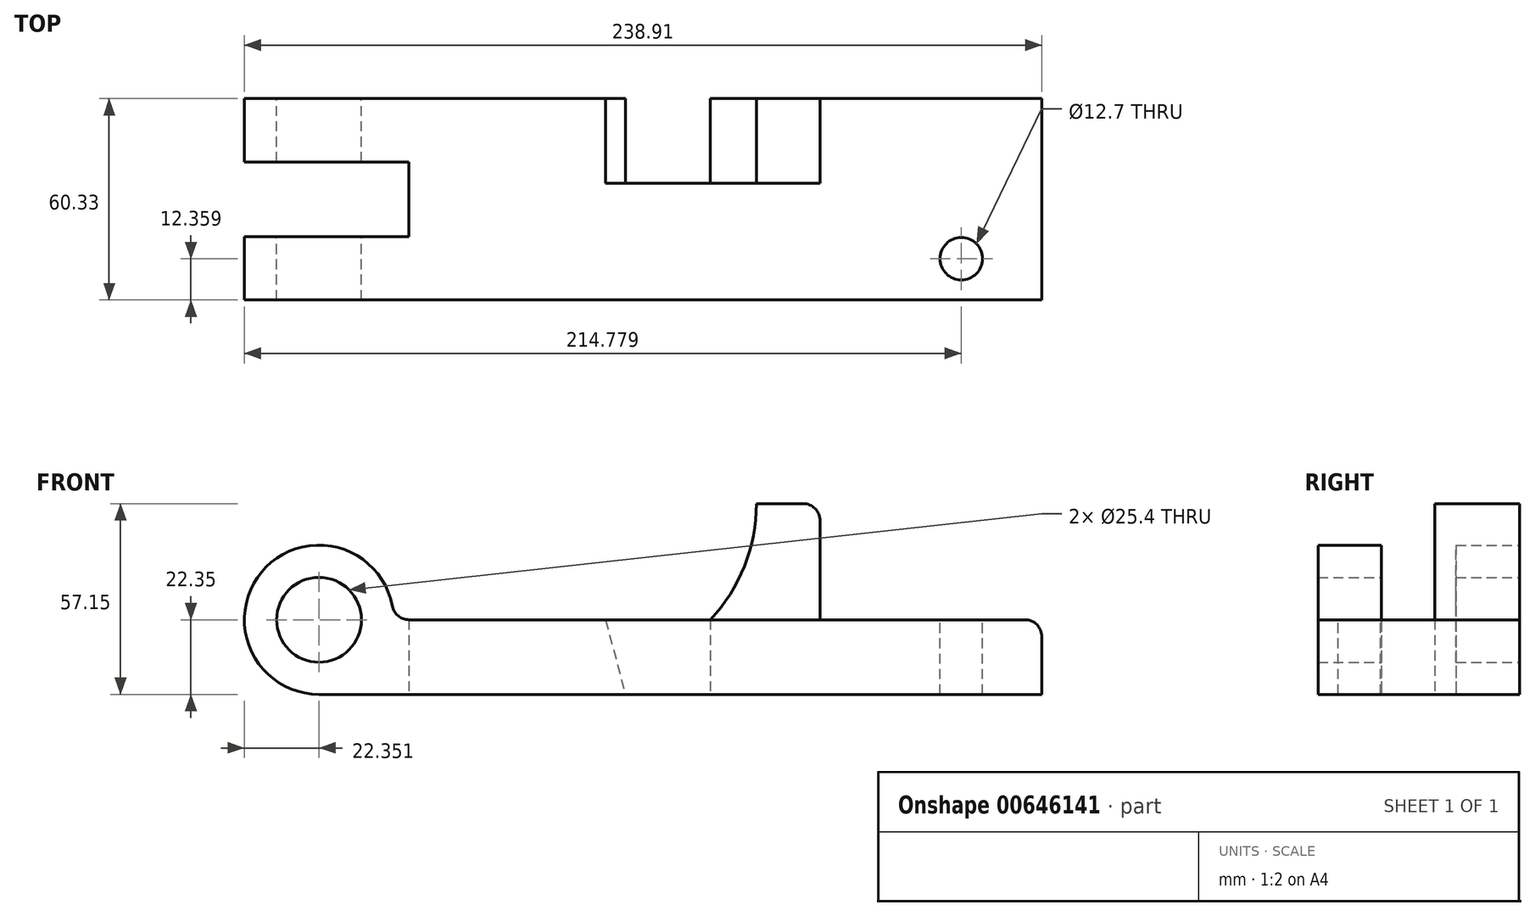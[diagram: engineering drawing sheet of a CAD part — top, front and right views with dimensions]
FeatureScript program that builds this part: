
annotation { "Feature Type Name" : "Feature", "Feature Type Description" : "" }
export const myFeature = defineFeature(function(context is Context, id is Id, definition is map)
    precondition{}
    {
        {
            var Q0;
            Q0=qCreatedBy(makeId("Front.planeOp"),FACE);
            var sketch = newSketch(context, id + "F0", { "sketchPlane" : qUnion([Q0])});
            skCircle(sketch, "E0", {"center": v(-45.26, 0) * mm, "radius": 22.35 * mm});
            skCircle(sketch, "E1", {"center": v(-45.26, 0) * mm, "radius": 12.7 * mm});
            skLineSegment(sketch, "E2", {"start": v(-45.26, -22.35) * mm, "end": v(71.99, -22.35) * mm});
            skLineSegment(sketch, "E3", {"start": v(-45.26, -22.35) * mm, "end": v(171.3, -22.35) * mm});
            skLineSegment(sketch, "E4", {"start": v(171.3, -22.35) * mm, "end": v(171.3, 0) * mm});
            skLineSegment(sketch, "E5", {"start": v(171.3, 0) * mm, "end": v(104.83, 0) * mm});
            skLineSegment(sketch, "E6", {"start": v(104.83, 0) * mm, "end": v(104.83, 34.8) * mm});
            skLineSegment(sketch, "E7", {"start": v(104.83, 34.8) * mm, "end": v(85.78, 34.8) * mm});
            skLineSegment(sketch, "E8", {"start": v(-45.26, 0) * mm, "end": v(71.99, 0) * mm});
            skArc(sketch, "E9", {"start": v(71.99, 0) * mm, "mid": v(82.2, 16.08) * mm, "end": v(85.78, 34.8) * mm});
            skLineSegment(sketch, "E10", {"start": v(71.99, 0) * mm, "end": v(104.83, 0) * mm});
            skLineSegment(sketch, "E11", {"start": v(71.99, -22.35) * mm, "end": v(46.54, -22.35) * mm});
            skLineSegment(sketch, "E12", {"start": v(71.99, 0) * mm, "end": v(40.6, 0) * mm});
            skLineSegment(sketch, "E13", {"start": v(40.6, 0) * mm, "end": v(46.54, -22.35) * mm});
            skLineSegment(sketch, "E14", {"start": v(71.99, 0) * mm, "end": v(71.99, -22.35) * mm});
            skSolve(sketch);
        }
        {
            var Q0;
            Q0=makeQuery(id+"F0.imprint","IMPRINT",FACE,{"disambiguationData":[TD([[makeQuery(id+"F0.imprint","IMPRINT",EDGE,{"derivedFrom":sQuery(id+"F0.wireOp",EDGE,"E1")}),-1.0]])]});
            var Q1;
            {var subQ0=sQuery(id+"F0.wireOp",EDGE,"E4");Q1=makeQuery(id+"F0.imprint","IMPRINT",FACE,{"disambiguationData":[TD([[makeQuery(id+"F0.imprint","IMPRINT",EDGE,{"derivedFrom":subQ0}),1.0]])]});}
            var Q2;
            {var subQ5=sQuery(id+"F0.wireOp",EDGE,"E13");Q2=makeQuery(id+"F0.imprint","IMPRINT",FACE,{"disambiguationData":[TD([[makeQuery(id+"F0.imprint","IMPRINT",EDGE,{"derivedFrom":subQ5}),-1.0]])]});}
            var Q3;
            Q3=makeQuery(id+"F0.imprint","IMPRINT",FACE,{"disambiguationData":[TD([[makeQuery(id+"F0.imprint","IMPRINT",EDGE,{"derivedFrom":sQuery(id+"F0.wireOp",EDGE,"E13")}),1.0]])]});
            extrude(context, id + "F1", {"entities" : qUnion([Q0, Q1, Q2, Q3]), "depth" : 60.32 * mm, "offsetDistance" : 25.4 * mm});
        }
        {
            var Q0;
            Q0=makeQuery(id+"F1.opExtrude","SWEPT_EDGE",EDGE,{"disambiguationData":[OSD([sQuery(id+"F0.wireOp",EDGE,"E0"),sQuery(id+"F0.wireOp",EDGE,"E8")])]});
            var Q1;
            Q1=makeQuery(id+"F1.opExtrude","SWEPT_EDGE",EDGE,{"disambiguationData":[OSD([sQuery(id+"F0.wireOp",EDGE,"E5"),sQuery(id+"F0.wireOp",EDGE,"E6")])]});
            var Q2;
            Q2=makeQuery(id+"F1.opExtrude","SWEPT_EDGE",EDGE,{"disambiguationData":[OSD([sQuery(id+"F0.wireOp",EDGE,"E6"),sQuery(id+"F0.wireOp",EDGE,"E7")])]});
            var Q3;
            Q3=makeQuery(id+"F1.opExtrude","SWEPT_EDGE",EDGE,{"disambiguationData":[OSD([sQuery(id+"F0.wireOp",EDGE,"E4"),sQuery(id+"F0.wireOp",EDGE,"E5")])]});
            fillet(context, id + "F2", {"entities" : qUnion([Q0, Q1, Q2, Q3]), "radius" : 5.08 * mm, "tangentPropagation" : true, "allowEdgeOverflow" : false});
        }
        {
            var Q0;
            Q0=makeQuery(id+"F1.opExtrude","SWEPT_FACE",FACE,{"disambiguationData":[OSD([sQuery(id+"F0.wireOp",EDGE,"E8")])]});
            var sketch = newSketch(context, id + "F3", { "sketchPlane" : qUnion([Q0])});
            skLineSegment(sketch, "E15", {"start": v(-18.3, -60.33) * mm, "end": v(-18.3, -41.33) * mm});
            skLineSegment(sketch, "E16", {"start": v(-18.3, -41.33) * mm, "end": v(-70.9, -41.33) * mm});
            skLineSegment(sketch, "E17", {"start": v(-18.3, 0) * mm, "end": v(-18.3, -19) * mm});
            skLineSegment(sketch, "E18", {"start": v(-18.3, -19) * mm, "end": v(-70.9, -19) * mm});
            skLineSegment(sketch, "E19", {"start": v(-70.9, -19) * mm, "end": v(-70.9, -41.33) * mm});
            skLineSegment(sketch, "E20", {"start": v(-18.3, -19) * mm, "end": v(-18.3, -41.33) * mm});
            skSolve(sketch);
        }
        {
            var Q0;
            Q0=makeQuery(id+"F3.imprint","IMPRINT",FACE,{"disambiguationData":[TD([[makeQuery(id+"F3.imprint","IMPRINT",EDGE,{"derivedFrom":sQuery(id+"F3.wireOp",EDGE,"E16")}),-1.0]])]});
            extrude(context, id + "F4", {"entities" : qUnion([Q0]), "operationType" : NewBodyOperationType.REMOVE, "endBound" : BoundingType.SYMMETRIC, "depth" : 51.82 * mm, "offsetDistance" : 25.4 * mm});
        }
        {
            var Q0;
            Q0=makeQuery(id+"F0.imprint","IMPRINT",FACE,{"disambiguationData":[TD([[makeQuery(id+"F0.imprint","IMPRINT",EDGE,{"derivedFrom":sQuery(id+"F0.wireOp",EDGE,"E6")}),1.0]])]});
            extrude(context, id + "F5", {"entities" : qUnion([Q0]), "operationType" : NewBodyOperationType.ADD, "depth" : 25.4 * mm, "offsetDistance" : 25.4 * mm});
        }
        {
            var Q0;
            Q0=makeQuery(id+"F0.imprint","IMPRINT",FACE,{"disambiguationData":[TD([[makeQuery(id+"F0.imprint","IMPRINT",EDGE,{"derivedFrom":sQuery(id+"F0.wireOp",EDGE,"E13")}),1.0]])]});
            extrude(context, id + "F6", {"entities" : qUnion([Q0]), "operationType" : NewBodyOperationType.REMOVE, "depth" : 25.4 * mm, "offsetDistance" : 25.4 * mm});
        }
        {
            var Q0;
            Q0=makeQuery(id+"F5.opExtrude","SWEPT_EDGE",EDGE,{"disambiguationData":[OSD([sQuery(id+"F0.wireOp",EDGE,"E5"),sQuery(id+"F0.wireOp",EDGE,"E6"),sQuery(id+"F0.wireOp",EDGE,"E10")])]});
            var Q1;
            Q1=makeQuery(id+"F5.opExtrude","SWEPT_EDGE",EDGE,{"disambiguationData":[OSD([sQuery(id+"F0.wireOp",EDGE,"E6"),sQuery(id+"F0.wireOp",EDGE,"E7")])]});
            fillet(context, id + "F7", {"entities" : qUnion([Q0, Q1]), "radius" : 5.08 * mm, "tangentPropagation" : true, "allowEdgeOverflow" : false});
        }
        {
            var Q0;
            Q0=makeQuery(id+"F1.opExtrude","SWEPT_FACE",FACE,{"disambiguationData":[OSD([sQuery(id+"F0.wireOp",EDGE,"E5"),sQuery(id+"F0.wireOp",EDGE,"E8"),sQuery(id+"F0.wireOp",EDGE,"E10"),sQuery(id+"F0.wireOp",EDGE,"E12")])]});
            var sketch = newSketch(context, id + "F8", { "sketchPlane" : qUnion([Q0])});
            skCircle(sketch, "E21", {"center": v(147.17, -47.97) * mm, "radius": 6.35 * mm});
            skSolve(sketch);
        }
        {
            var Q0;
            Q0=makeQuery(id+"F8.imprint","IMPRINT",FACE,{"disambiguationData":[TD([[makeQuery(id+"F8.imprint","IMPRINT",EDGE,{"derivedFrom":sQuery(id+"F8.wireOp",EDGE,"E21")}),1.0]])]});
            extrude(context, id + "F9", {"entities" : qUnion([Q0]), "operationType" : NewBodyOperationType.REMOVE, "oppositeDirection" : true, "depth" : 25.4 * mm, "offsetDistance" : 25.4 * mm});
        }
    });
